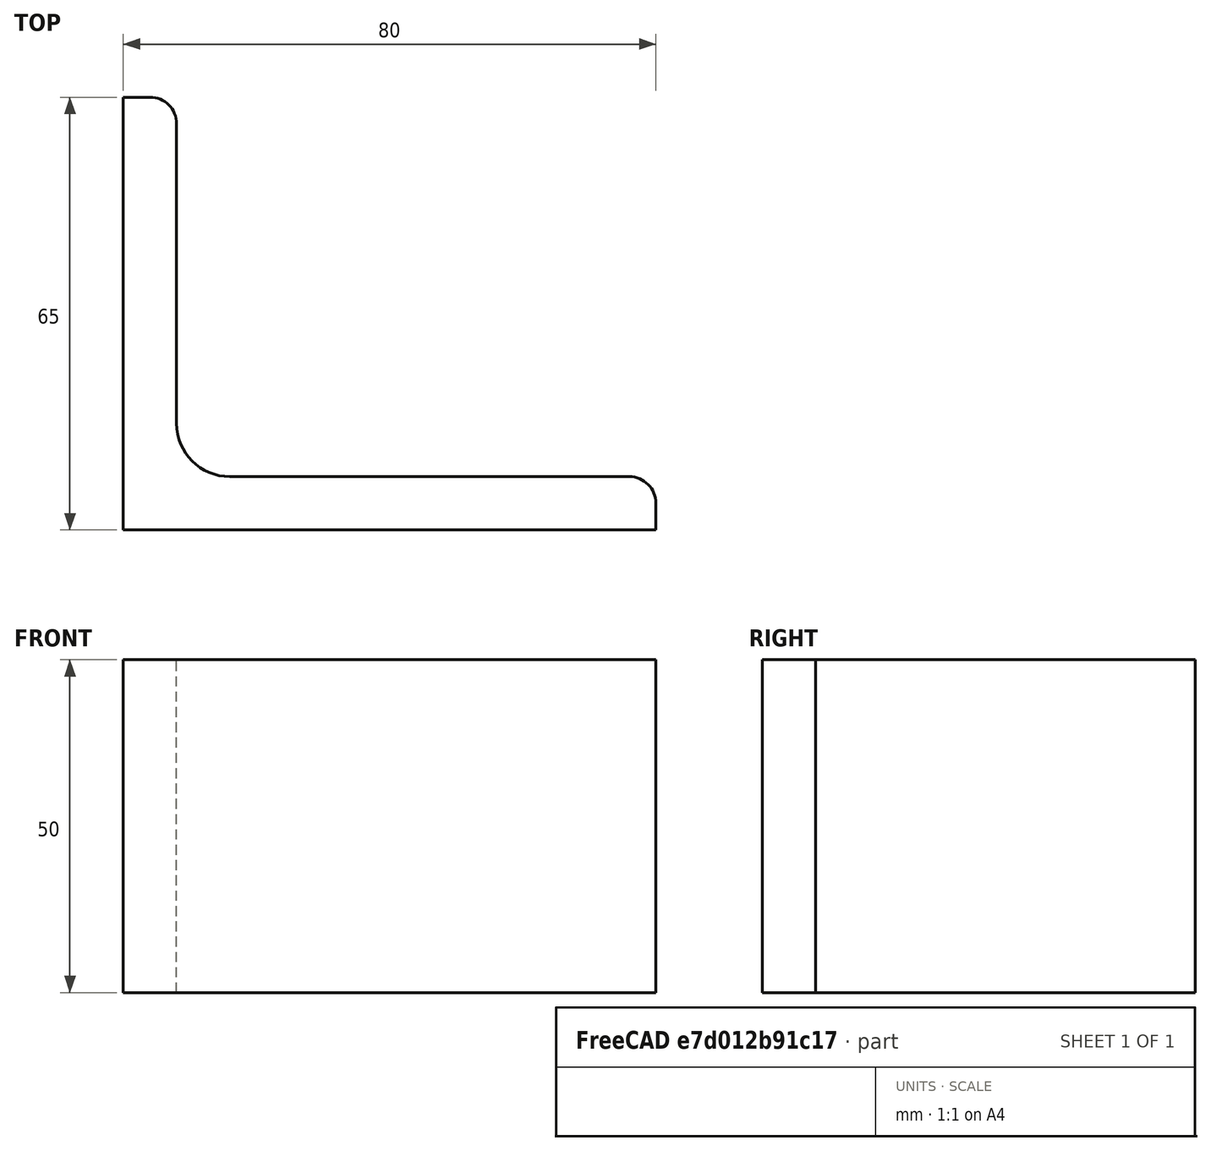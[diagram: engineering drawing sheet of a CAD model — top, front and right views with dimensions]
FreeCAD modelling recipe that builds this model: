
FCSTD DOCUMENT  (FreeCAD 0.15R4671 (Git))
Label: Angle Bar 80x65x8 EN10056 S235JR
License: All rights reserved
LicenseURL: http://en.wikipedia.org/wiki/All_rights_reserved
objects: Sketcher::SketchObject×1, Part::Extrusion×1
note: 2 computed .brp shape members not serialized (recipe doc carries the construction recipe); baked Part::Feature solids carry a one-line shape summary decoded from their .brp

FEATURE [Sketcher::SketchObject] Sketch
  sketch-geometry (9):
    g0: LineSegment StartX=0 StartY=0 StartZ=0 EndX=80 EndY=0 EndZ=0
    g1: LineSegment StartX=80 StartY=0 StartZ=0 EndX=80 EndY=4 EndZ=0
    g2: LineSegment StartX=76 StartY=8 StartZ=0 EndX=16 EndY=8 EndZ=0
    g3: LineSegment StartX=0 StartY=0 StartZ=0 EndX=0 EndY=65 EndZ=0
    g4: LineSegment StartX=0 StartY=65 StartZ=0 EndX=4 EndY=65 EndZ=0
    g5: LineSegment StartX=8 StartY=61 StartZ=0 EndX=8 EndY=16 EndZ=0
    g6: ArcOfCircle CenterX=16 CenterY=16 CenterZ=0 NormalX=0 NormalY=0 NormalZ=1 Radius=8 StartAngle=3.14159 EndAngle=4.71239
    g7: ArcOfCircle CenterX=4 CenterY=61 CenterZ=0 NormalX=0 NormalY=0 NormalZ=1 Radius=4 StartAngle=0 EndAngle=1.5708
    g8: ArcOfCircle CenterX=76 CenterY=4 CenterZ=0 NormalX=0 NormalY=0 NormalZ=1 Radius=4 StartAngle=0 EndAngle=1.5708
  constraints (23):
    c: Coincident(g0,g-1)
    c: Horizontal(g0)
    c: Coincident(g1,g0)
    c: Vertical(g1)
    c: Horizontal(g2)
    c: Coincident(g3,g-1)
    c: Vertical(g3)
    c: Coincident(g4,g3)
    c: Horizontal(g4)
    c: Vertical(g5)
    c: Tangent(g5,g6) = -1.5708
    c: Tangent(g2,g6) = 1.5708
    c: Tangent(g4,g7) = 1.5708
    c: Tangent(g5,g7) = 1.5708
    c: Tangent(g2,g8) = -1.5708
    c: Tangent(g1,g8) = -1.5708
    c: DistanceX(g0) = 80
    c: DistanceY(g3) = 65
    c: DistanceY(g0,g2) = 8
    c: DistanceX(g3,g5) = 8
    c: Radius(g6) = 8
    c: Radius(g8) = 4
    c: Radius(g7) = 4
FEATURE [Part::Extrusion] Extrude  label="Angle Bar 80x65x8 EN10056 S235JR"
  Base = -> Sketch
  Dir = (0,0,50)
  Solid = true
